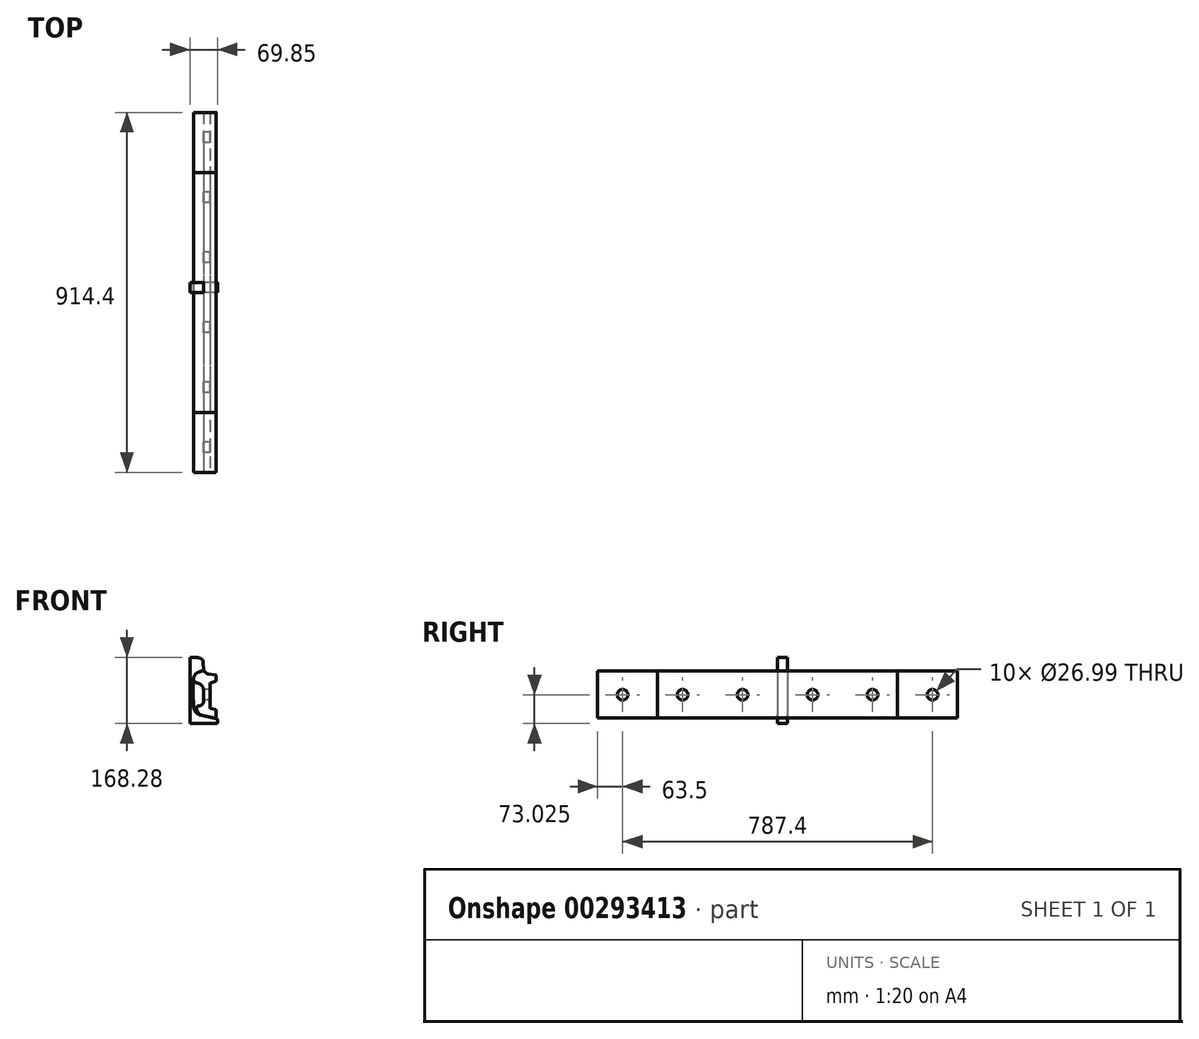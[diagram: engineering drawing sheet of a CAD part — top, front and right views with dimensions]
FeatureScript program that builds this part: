
annotation { "Feature Type Name" : "Feature", "Feature Type Description" : "" }
export const myFeature = defineFeature(function(context is Context, id is Id, definition is map)
    precondition{}
    {
        {
            var Q0;
            Q0=qCreatedBy(makeId("Front.planeOp"),FACE);
            var sketch = newSketch(context, id + "F0", { "sketchPlane" : qUnion([Q0])});
            skLineSegment(sketch, "E0", {"start": v(0, 183.43) * mm, "end": v(0, -103.17) * mm, "construction": true});
            skLineSegment(sketch, "E1", {"start": v(0, 0) * mm, "end": v(68.26, 0) * mm});
            skLineSegment(sketch, "E2", {"start": v(69.85, 1.59) * mm, "end": v(69.85, 9.87) * mm});
            skLineSegment(sketch, "E3", {"start": v(68.65, 11.41) * mm, "end": v(24.96, 22.33) * mm});
            skArc(sketch, "E4", {"start": v(68.26, 0) * mm, "mid": v(69.39, 0.46) * mm, "end": v(69.85, 1.59) * mm});
            skArc(sketch, "E5", {"start": v(69.85, 9.87) * mm, "mid": v(69.51, 10.85) * mm, "end": v(68.65, 11.41) * mm});
            skArc(sketch, "E6", {"start": v(10.68, 38.45) * mm, "mid": v(15.33, 28.18) * mm, "end": v(24.96, 22.33) * mm});
            skArc(sketch, "E7", {"start": v(7.94, 82.55) * mm, "mid": v(8.62, 60.46) * mm, "end": v(10.68, 38.45) * mm});
            skArc(sketch, "E8", {"start": v(8.85, 107.95) * mm, "mid": v(8.16, 95.26) * mm, "end": v(7.94, 82.55) * mm});
            skArc(sketch, "E9", {"start": v(9.93, 116.42) * mm, "mid": v(9.27, 112.2) * mm, "end": v(8.85, 107.95) * mm});
            skLineSegment(sketch, "E10", {"start": v(-29.08, 125.41) * mm, "end": v(76.53, 125.41) * mm, "construction": true});
            skArc(sketch, "E11", {"start": v(15.87, 167.78) * mm, "mid": v(7.94, 168.15) * mm, "end": v(0, 168.27) * mm});
            skArc(sketch, "E12", {"start": v(28.14, 164.92) * mm, "mid": v(22.13, 166.86) * mm, "end": v(15.87, 167.78) * mm});
            skArc(sketch, "E13", {"start": v(34, 156.37) * mm, "mid": v(32.34, 161.51) * mm, "end": v(28.14, 164.92) * mm});
            skArc(sketch, "E14", {"start": v(33.33, 133.74) * mm, "mid": v(34.2, 134.32) * mm, "end": v(34.53, 135.32) * mm});
            skLineSegment(sketch, "E15", {"start": v(34, 156.37) * mm, "end": v(34.53, 135.32) * mm});
            skArc(sketch, "E16", {"start": v(24.04, 131.42) * mm, "mid": v(14.78, 126) * mm, "end": v(9.93, 116.42) * mm});
            skLineSegment(sketch, "E17", {"start": v(24.04, 131.42) * mm, "end": v(33.33, 133.74) * mm});
            skLineSegment(sketch, "E18", {"start": v(34.53, 164.1) * mm, "end": v(34.53, 130.1) * mm, "construction": true});
            skLineSegment(sketch, "E19", {"start": v(2.79, 73.03) * mm, "end": v(165.83, 73.03) * mm, "construction": true});
            skPoint(sketch, "E20", {"position": v(8.07, 73.03) * mm});
            skLineSegment(sketch, "E21", {"start": v(0, 28.57) * mm, "end": v(68.65, 11.41) * mm, "construction": true});
            skLineSegment(sketch, "E22", {"start": v(-14.61, 82.55) * mm, "end": v(613.53, 82.55) * mm, "construction": true});
            skLineSegment(sketch, "E23", {"start": v(0, 125.41) * mm, "end": v(72.4, 143.51) * mm, "construction": true});
            skLineSegment(sketch, "E24", {"start": v(0, 168.27) * mm, "end": v(0, 0) * mm});
            skSolve(sketch);
        }
        {
            var Q0;
            Q0=qSketchRegion(id+"F0",true);
            extrude(context, id + "F1", {"entities" : qUnion([Q0]), "oppositeDirection" : true, "depth" : 25.4 * mm});
        }
        {
            var Q0;
            Q0=qCreatedBy(makeId("Front.planeOp"),FACE);
            var sketch = newSketch(context, id + "F2", { "sketchPlane" : qUnion([Q0])});
            skLineSegment(sketch, "E25", {"start": v(50.8, 100.01) * mm, "end": v(50.8, 41.26) * mm});
            skLineSegment(sketch, "E26", {"start": v(34.92, 84.13) * mm, "end": v(34.92, 57.15) * mm});
            skArc(sketch, "E27", {"start": v(34.92, 84.13) * mm, "mid": v(30.1, 96.8) * mm, "end": v(18.06, 103.06) * mm});
            skArc(sketch, "E28", {"start": v(9.63, 112.1) * mm, "mid": v(12.18, 106.02) * mm, "end": v(18.06, 103.06) * mm});
            skArc(sketch, "E29", {"start": v(24.04, 131.42) * mm, "mid": v(13.39, 124.33) * mm, "end": v(9.63, 112.1) * mm});
            skArc(sketch, "E30", {"start": v(52.89, 103) * mm, "mid": v(51.37, 101.83) * mm, "end": v(50.8, 100.01) * mm});
            skArc(sketch, "E31", {"start": v(64.59, 107.25) * mm, "mid": v(66.1, 108.42) * mm, "end": v(66.67, 110.24) * mm});
            skLineSegment(sketch, "E32", {"start": v(52.89, 103) * mm, "end": v(64.59, 107.25) * mm});
            skLineSegment(sketch, "E33", {"start": v(66.67, 110.24) * mm, "end": v(66.67, 120.83) * mm});
            skArc(sketch, "E34", {"start": v(66.67, 120.83) * mm, "mid": v(65.84, 122.98) * mm, "end": v(63.78, 124) * mm});
            skLineSegment(sketch, "E35", {"start": v(47.07, 125.46) * mm, "end": v(63.78, 124) * mm});
            skArc(sketch, "E36", {"start": v(22.27, 44.45) * mm, "mid": v(31.22, 48.19) * mm, "end": v(34.92, 57.15) * mm});
            skArc(sketch, "E37", {"start": v(50.8, 41.26) * mm, "mid": v(51.47, 39.3) * mm, "end": v(53.2, 38.18) * mm});
            skLineSegment(sketch, "E38", {"start": v(53.2, 38.18) * mm, "end": v(64.27, 35.42) * mm});
            skArc(sketch, "E39", {"start": v(66.68, 32.34) * mm, "mid": v(66, 34.3) * mm, "end": v(64.27, 35.42) * mm});
            skLineSegment(sketch, "E40", {"start": v(66.68, 32.34) * mm, "end": v(66.68, 17.36) * mm});
            skArc(sketch, "E41", {"start": v(63.26, 14.2) * mm, "mid": v(65.66, 15.03) * mm, "end": v(66.68, 17.36) * mm});
            skArc(sketch, "E42", {"start": v(16.74, 38.7) * mm, "mid": v(20.84, 27.53) * mm, "end": v(30.77, 20.97) * mm});
            skArc(sketch, "E43", {"start": v(22.27, 44.45) * mm, "mid": v(18.3, 42.75) * mm, "end": v(16.74, 38.7) * mm});
            skLineSegment(sketch, "E44", {"start": v(16.45, 47.49) * mm, "end": v(16.96, 32.2) * mm, "construction": true});
            skLineSegment(sketch, "E45", {"start": v(9.98, 50.84) * mm, "end": v(10.68, 29.85) * mm, "construction": true});
            skArc(sketch, "E46.0.0", {"start": v(9.93, 116.42) * mm, "mid": v(14.78, 126) * mm, "end": v(24.04, 131.42) * mm});
            skLineSegment(sketch, "E46.0.1", {"start": v(24.04, 131.42) * mm, "end": v(33.33, 133.74) * mm});
            skArc(sketch, "E46.0.2", {"start": v(33.33, 133.74) * mm, "mid": v(34.2, 134.32) * mm, "end": v(34.53, 135.32) * mm});
            skLineSegment(sketch, "E46.0.3", {"start": v(34.53, 135.32) * mm, "end": v(34, 156.37) * mm});
            skArc(sketch, "E46.0.4", {"start": v(34, 156.37) * mm, "mid": v(32.34, 161.51) * mm, "end": v(28.14, 164.92) * mm});
            skArc(sketch, "E46.0.5", {"start": v(28.14, 164.92) * mm, "mid": v(22.13, 166.86) * mm, "end": v(15.87, 167.78) * mm});
            skArc(sketch, "E46.0.6", {"start": v(15.87, 167.78) * mm, "mid": v(7.94, 168.15) * mm, "end": v(0, 168.27) * mm});
            skLineSegment(sketch, "E46.0.7", {"start": v(0, 168.27) * mm, "end": v(0, 0) * mm});
            skLineSegment(sketch, "E46.0.8", {"start": v(0, 0) * mm, "end": v(68.26, 0) * mm});
            skArc(sketch, "E46.0.9", {"start": v(68.26, 0) * mm, "mid": v(69.39, 0.46) * mm, "end": v(69.85, 1.59) * mm});
            skLineSegment(sketch, "E46.0.10", {"start": v(69.85, 1.59) * mm, "end": v(69.85, 9.87) * mm});
            skArc(sketch, "E46.0.11", {"start": v(69.85, 9.87) * mm, "mid": v(69.51, 10.85) * mm, "end": v(68.65, 11.41) * mm});
            skLineSegment(sketch, "E46.0.12", {"start": v(68.65, 11.41) * mm, "end": v(24.96, 22.33) * mm});
            skArc(sketch, "E46.0.13", {"start": v(24.96, 22.33) * mm, "mid": v(15.33, 28.18) * mm, "end": v(10.68, 38.45) * mm});
            skArc(sketch, "E46.0.14", {"start": v(10.68, 38.45) * mm, "mid": v(8.06, 73.16) * mm, "end": v(8.85, 107.95) * mm});
            skArc(sketch, "E46.0.15", {"start": v(8.85, 107.95) * mm, "mid": v(9.27, 112.2) * mm, "end": v(9.93, 116.42) * mm});
            skArc(sketch, "E47", {"start": v(53.82, 15.5) * mm, "mid": v(58.52, 14.7) * mm, "end": v(63.26, 14.2) * mm});
            skPoint(sketch, "E48", {"position": v(38.1, 19.05) * mm});
            skLineSegment(sketch, "E49", {"start": v(128.97, 382.53) * mm, "end": v(34.13, 3.17) * mm, "construction": true});
            skArc(sketch, "E50", {"start": v(30.77, 20.97) * mm, "mid": v(42.25, 18.04) * mm, "end": v(53.82, 15.5) * mm});
            skPoint(sketch, "E51", {"position": v(34.13, 0) * mm});
            skLineSegment(sketch, "E52", {"start": v(47.07, 125.46) * mm, "end": v(80.4, 125.46) * mm, "construction": true});
            skLineSegment(sketch, "E53", {"start": v(52.89, 103) * mm, "end": v(82.99, 103) * mm, "construction": true});
            skLineSegment(sketch, "E54", {"start": v(-13.94, 77) * mm, "end": v(125.71, 77) * mm, "construction": true});
            skLineSegment(sketch, "E55", {"start": v(24.04, 131.42) * mm, "end": v(35.5, 131.42) * mm, "construction": true});
            skLineSegment(sketch, "E56", {"start": v(24.04, 131.42) * mm, "end": v(30.2, 132.96) * mm});
            skArc(sketch, "E57", {"start": v(40.2, 129.33) * mm, "mid": v(35.76, 132.68) * mm, "end": v(30.2, 132.96) * mm});
            skArc(sketch, "E58", {"start": v(40.2, 129.33) * mm, "mid": v(43.22, 126.65) * mm, "end": v(47.07, 125.46) * mm});
            skSolve(sketch);
        }
        {
            var Q0;
            Q0=qCreatedBy(makeId("Right.planeOp"),FACE);
            cPlane(context, id + "F3", {"entities" : qUnion([Q0]), "cplaneType" : CPlaneType.OFFSET, "offset" : 76.2 * mm, "width" : 152.4 * mm, "height" : 152.4 * mm});
        }
        {
            var Q0;
            Q0=qCreatedBy(id+"F3.planeOp",FACE);
            var sketch = newSketch(context, id + "F4", { "sketchPlane" : qUnion([Q0])});
            skPoint(sketch, "E59", {"position": v(88.9, 73.03) * mm});
            skPoint(sketch, "E60", {"position": v(241.3, 73.03) * mm});
            skPoint(sketch, "E61", {"position": v(393.7, 73.03) * mm});
            skLineSegment(sketch, "E62", {"start": v(0, 107.71) * mm, "end": v(0, -101.75) * mm, "construction": true});
            skPoint(sketch, "E63.MirrorP", {"position": v(-393.7, 73.02) * mm});
            skPoint(sketch, "E64.MirrorP", {"position": v(-241.3, 73.02) * mm});
            skPoint(sketch, "E65.MirrorP", {"position": v(-88.9, 73.02) * mm});
            skSolve(sketch);
        }
        {
            var Q0;
            Q0=makeQuery(id+"F2.imprint","IMPRINT",FACE,{"disambiguationData":[TD([[makeQuery(id+"F2.imprint","IMPRINT",EDGE,{"derivedFrom":sQuery(id+"F2.wireOp",EDGE,"E25")}),-1.0]])]});
            extrude(context, id + "F5", {"entities" : qUnion([Q0]), "oppositeDirection" : true, "depth" : 609.6 * mm, "symmetric" : true});
        }
        {
            var Q0;
            Q0=sQuery(id+"F4.wireOp",VERTEX,"E64.MirrorP");
            var Q1;
            Q1=sQuery(id+"F4.wireOp",VERTEX,"E65.MirrorP");
            var Q2;
            Q2=sQuery(id+"F4.wireOp",VERTEX,"E59");
            var Q3;
            Q3=sQuery(id+"F4.wireOp",VERTEX,"E60");
            var Q4;
            Q4=makeQuery(id+"F5.opExtrude","SWEPT_BODY",BODY,{"disambiguationData":[OSD([sQuery(id+"F2.wireOp",EDGE,"E25"),sQuery(id+"F2.wireOp",EDGE,"E26"),sQuery(id+"F2.wireOp",EDGE,"E27"),sQuery(id+"F2.wireOp",EDGE,"E28"),sQuery(id+"F2.wireOp",EDGE,"E29"),sQuery(id+"F2.wireOp",EDGE,"E30"),sQuery(id+"F2.wireOp",EDGE,"E31"),sQuery(id+"F2.wireOp",EDGE,"E32"),sQuery(id+"F2.wireOp",EDGE,"E33"),sQuery(id+"F2.wireOp",EDGE,"E34"),sQuery(id+"F2.wireOp",EDGE,"E35"),sQuery(id+"F2.wireOp",EDGE,"E36"),sQuery(id+"F2.wireOp",EDGE,"E37"),sQuery(id+"F2.wireOp",EDGE,"E38"),sQuery(id+"F2.wireOp",EDGE,"E39"),sQuery(id+"F2.wireOp",EDGE,"E40"),sQuery(id+"F2.wireOp",EDGE,"E41"),sQuery(id+"F2.wireOp",EDGE,"E42"),sQuery(id+"F2.wireOp",EDGE,"E43"),sQuery(id+"F2.wireOp",EDGE,"E46.0.0"),sQuery(id+"F2.wireOp",EDGE,"E47"),sQuery(id+"F2.wireOp",EDGE,"E50"),sQuery(id+"F2.wireOp",EDGE,"E56"),sQuery(id+"F2.wireOp",EDGE,"E57"),sQuery(id+"F2.wireOp",EDGE,"E58")])]});
            hole(context, id + "F6", {"style" : HoleStyle.SIMPLE, "endStyle" : HoleEndStyle.THROUGH, "holeDiameter" : 26.99 * mm, "tappedDepth" : 12.7 * mm, "tapClearance" : 3, "locations" : qUnion([Q0, Q1, Q2, Q3]), "scope" : qUnion([Q4])});
        }
        {
            var Q0;
            Q0=makeQuery(id+"F2.imprint","IMPRINT",FACE,{"disambiguationData":[TD([[makeQuery(id+"F2.imprint","IMPRINT",EDGE,{"derivedFrom":sQuery(id+"F2.wireOp",EDGE,"E25")}),-1.0]])]});
            extrude(context, id + "F7", {"entities" : qUnion([Q0]), "oppositeDirection" : true, "depth" : 914.4 * mm, "symmetric" : true});
        }
        {
            var Q0;
            Q0=sQuery(id+"F4.wireOp",VERTEX,"E63.MirrorP");
            var Q1;
            Q1=sQuery(id+"F4.wireOp",VERTEX,"E64.MirrorP");
            var Q2;
            Q2=sQuery(id+"F4.wireOp",VERTEX,"E65.MirrorP");
            var Q3;
            Q3=sQuery(id+"F4.wireOp",VERTEX,"E59");
            var Q4;
            Q4=sQuery(id+"F4.wireOp",VERTEX,"E60");
            var Q5;
            Q5=sQuery(id+"F4.wireOp",VERTEX,"E61");
            var Q6;
            Q6=makeQuery(id+"F7.opExtrude","SWEPT_BODY",BODY,{"disambiguationData":[OSD([sQuery(id+"F2.wireOp",EDGE,"E25"),sQuery(id+"F2.wireOp",EDGE,"E26"),sQuery(id+"F2.wireOp",EDGE,"E27"),sQuery(id+"F2.wireOp",EDGE,"E28"),sQuery(id+"F2.wireOp",EDGE,"E29"),sQuery(id+"F2.wireOp",EDGE,"E30"),sQuery(id+"F2.wireOp",EDGE,"E31"),sQuery(id+"F2.wireOp",EDGE,"E32"),sQuery(id+"F2.wireOp",EDGE,"E33"),sQuery(id+"F2.wireOp",EDGE,"E34"),sQuery(id+"F2.wireOp",EDGE,"E35"),sQuery(id+"F2.wireOp",EDGE,"E36"),sQuery(id+"F2.wireOp",EDGE,"E37"),sQuery(id+"F2.wireOp",EDGE,"E38"),sQuery(id+"F2.wireOp",EDGE,"E39"),sQuery(id+"F2.wireOp",EDGE,"E40"),sQuery(id+"F2.wireOp",EDGE,"E41"),sQuery(id+"F2.wireOp",EDGE,"E42"),sQuery(id+"F2.wireOp",EDGE,"E43"),sQuery(id+"F2.wireOp",EDGE,"E46.0.0"),sQuery(id+"F2.wireOp",EDGE,"E47"),sQuery(id+"F2.wireOp",EDGE,"E50"),sQuery(id+"F2.wireOp",EDGE,"E56"),sQuery(id+"F2.wireOp",EDGE,"E57"),sQuery(id+"F2.wireOp",EDGE,"E58")])]});
            hole(context, id + "F8", {"style" : HoleStyle.SIMPLE, "endStyle" : HoleEndStyle.THROUGH, "holeDiameter" : 26.99 * mm, "tappedDepth" : 12.7 * mm, "tapClearance" : 3, "locations" : qUnion([Q0, Q1, Q2, Q3, Q4, Q5]), "scope" : qUnion([Q6])});
        }
    });
